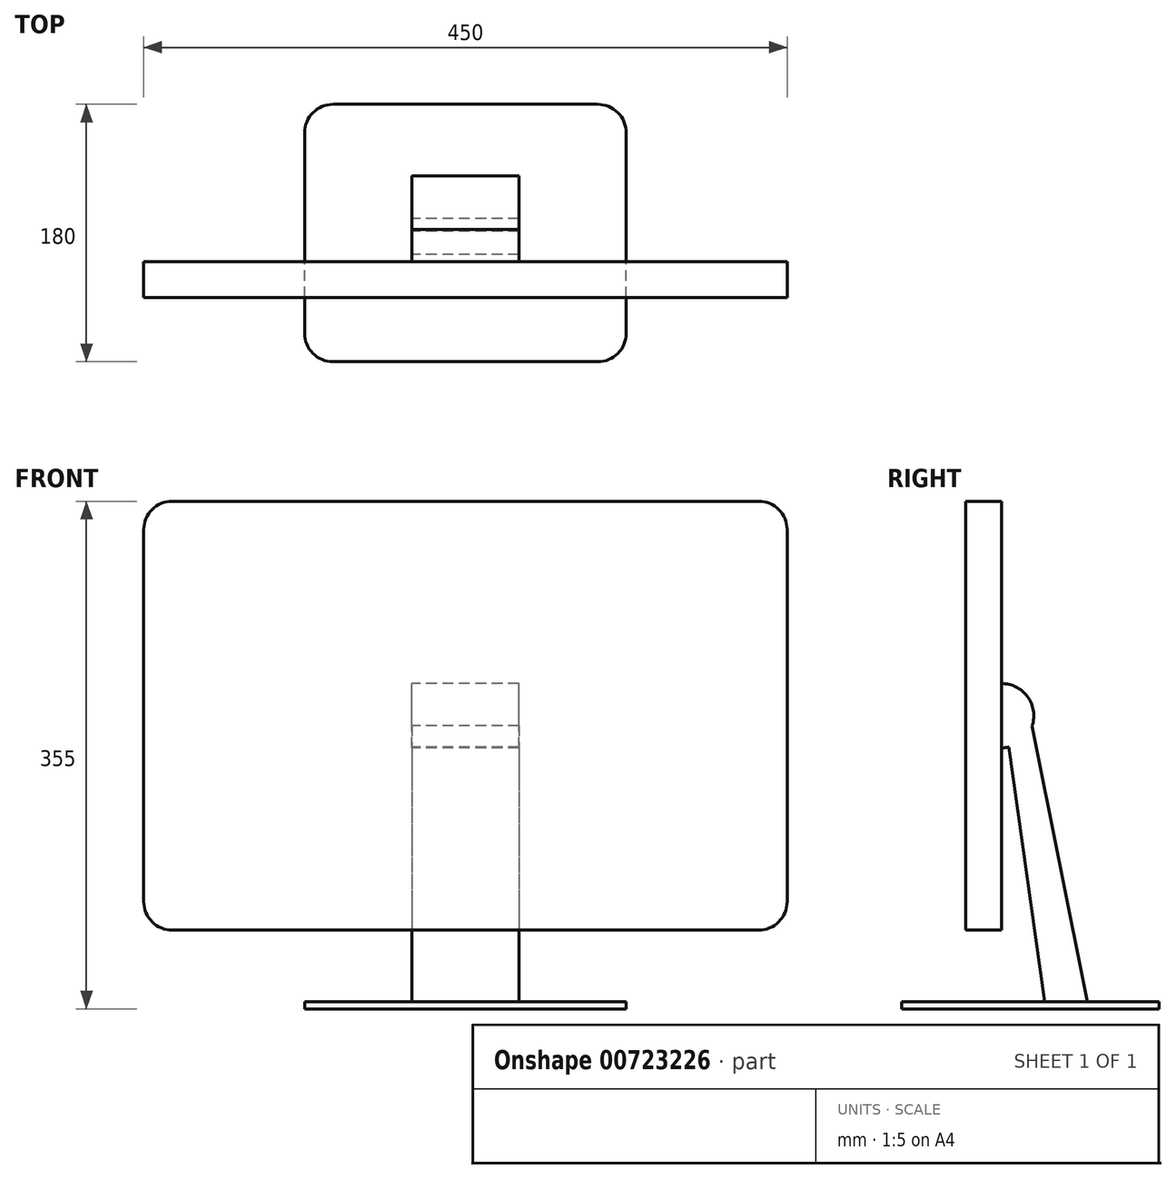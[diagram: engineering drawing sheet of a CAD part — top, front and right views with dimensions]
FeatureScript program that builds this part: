
annotation { "Feature Type Name" : "Feature", "Feature Type Description" : "" }
export const myFeature = defineFeature(function(context is Context, id is Id, definition is map)
    precondition{}
    {
        {
            var Q0;
            Q0=qCreatedBy(makeId("Front.planeOp"),FACE);
            var sketch = newSketch(context, id + "F0", { "sketchPlane" : qUnion([Q0])});
            skLineSegment(sketch, "E0.bottom", {"start": v(-205, 150) * mm, "end": v(205, 150) * mm});
            skLineSegment(sketch, "E0.top", {"start": v(-205, -150) * mm, "end": v(205, -150) * mm});
            skLineSegment(sketch, "E0.left", {"start": v(-225, 130) * mm, "end": v(-225, -130) * mm});
            skLineSegment(sketch, "E0.right", {"start": v(225, 130) * mm, "end": v(225, -130) * mm});
            skPoint(sketch, "E1.visualSharp", {"position": v(-225, -150) * mm});
            skArc(sketch, "E1.filletArc", {"start": v(-225, -130) * mm, "mid": v(-219.14, -144.14) * mm, "end": v(-205, -150) * mm});
            skPoint(sketch, "E2.visualSharp", {"position": v(-225, 150) * mm});
            skArc(sketch, "E2.filletArc", {"start": v(-205, 150) * mm, "mid": v(-219.14, 144.14) * mm, "end": v(-225, 130) * mm});
            skPoint(sketch, "E3.visualSharp", {"position": v(225, 150) * mm});
            skArc(sketch, "E3.filletArc", {"start": v(225, 130) * mm, "mid": v(219.14, 144.14) * mm, "end": v(205, 150) * mm});
            skPoint(sketch, "E4.visualSharp", {"position": v(225, -150) * mm});
            skArc(sketch, "E4.filletArc", {"start": v(205, -150) * mm, "mid": v(219.14, -144.14) * mm, "end": v(225, -130) * mm});
            skSolve(sketch);
        }
        {
            var Q0;
            Q0 = qSketchRegion(id + "F0", true);
            extrude(context, id + "F1", {"entities" : qUnion([Q0]), "depth" : 25 * mm, "offsetDistance" : 25 * mm});
        }
        {
            var Q0;
            Q0=qCreatedBy(makeId("Right.planeOp"),FACE);
            var sketch = newSketch(context, id + "F2", { "sketchPlane" : qUnion([Q0])});
            skArc(sketch, "E5", {"start": v(21.4, -6.94) * mm, "mid": v(-15.26, 16.54) * mm, "end": v(5.19, -21.9) * mm});
            skLineSegment(sketch, "E6", {"start": v(21.4, -6.94) * mm, "end": v(60, -200) * mm});
            skLineSegment(sketch, "E7", {"start": v(5.19, -21.9) * mm, "end": v(30, -200) * mm});
            skLineSegment(sketch, "E8", {"start": v(60, -200) * mm, "end": v(30, -200) * mm});
            skSolve(sketch);
        }
        {
            var Q0;
            Q0 = qSketchRegion(id + "F2", true);
            extrude(context, id + "F3", {"entities" : qUnion([Q0]), "operationType" : NewBodyOperationType.ADD, "endBound" : BoundingType.SYMMETRIC, "depth" : 75 * mm, "offsetDistance" : 25 * mm});
        }
        {
            var Q0;
            Q0=makeQuery(id+"F3.opExtrude","SWEPT_FACE",FACE,{"disambiguationData":[OSD([sQuery(id+"F2.wireOp",EDGE,"E8")])]});
            var sketch = newSketch(context, id + "F4", { "sketchPlane" : qUnion([Q0])});
            skLineSegment(sketch, "E9.bottom", {"start": v(-92.5, 70) * mm, "end": v(92.5, 70) * mm});
            skLineSegment(sketch, "E9.top", {"start": v(-92.5, -110) * mm, "end": v(92.5, -110) * mm});
            skLineSegment(sketch, "E9.left", {"start": v(-112.5, 50) * mm, "end": v(-112.5, -90) * mm});
            skLineSegment(sketch, "E9.right", {"start": v(112.5, 50) * mm, "end": v(112.5, -90) * mm});
            skPoint(sketch, "E10.visualSharp", {"position": v(-112.5, 70) * mm});
            skArc(sketch, "E10.filletArc", {"start": v(-92.5, 70) * mm, "mid": v(-106.64, 64.14) * mm, "end": v(-112.5, 50) * mm});
            skPoint(sketch, "E11.visualSharp", {"position": v(112.5, 70) * mm});
            skArc(sketch, "E11.filletArc", {"start": v(112.5, 50) * mm, "mid": v(106.64, 64.14) * mm, "end": v(92.5, 70) * mm});
            skPoint(sketch, "E12.visualSharp", {"position": v(112.5, -110) * mm});
            skArc(sketch, "E12.filletArc", {"start": v(92.5, -110) * mm, "mid": v(106.64, -104.14) * mm, "end": v(112.5, -90) * mm});
            skPoint(sketch, "E13.visualSharp", {"position": v(-112.5, -110) * mm});
            skArc(sketch, "E13.filletArc", {"start": v(-112.5, -90) * mm, "mid": v(-106.64, -104.14) * mm, "end": v(-92.5, -110) * mm});
            skSolve(sketch);
        }
        {
            var Q0;
            Q0 = qSketchRegion(id + "F4", true);
            extrude(context, id + "F5", {"entities" : qUnion([Q0]), "operationType" : NewBodyOperationType.ADD, "depth" : 5 * mm, "offsetDistance" : 25 * mm});
        }
    });
